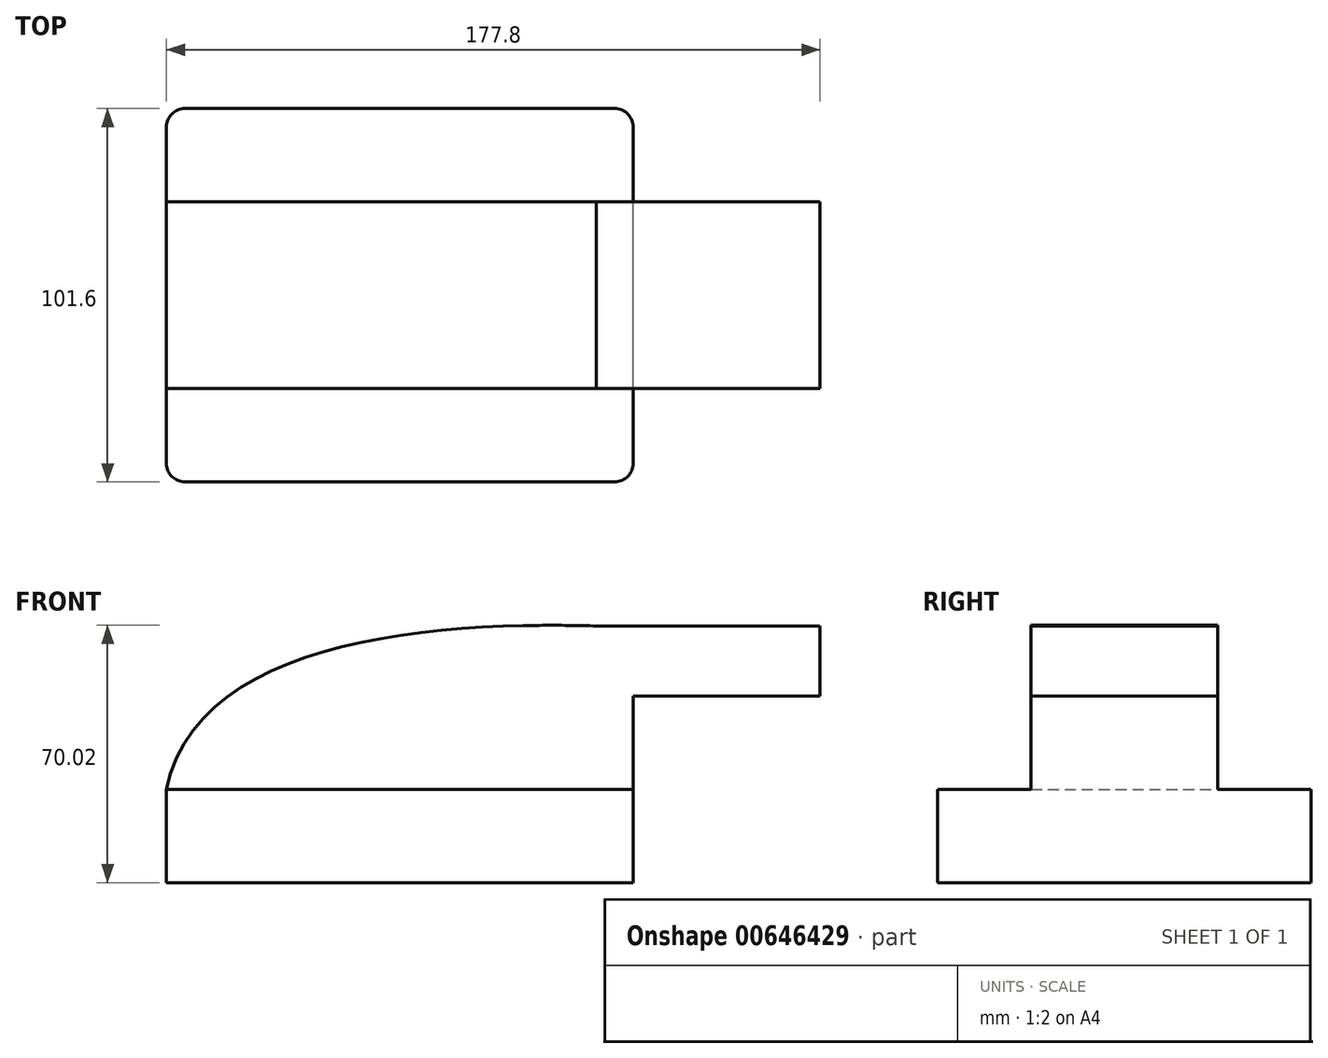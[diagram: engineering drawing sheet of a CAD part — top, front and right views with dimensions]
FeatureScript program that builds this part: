
annotation { "Feature Type Name" : "Feature", "Feature Type Description" : "" }
export const myFeature = defineFeature(function(context is Context, id is Id, definition is map)
    precondition{}
    {
        {
            var Q0;
            Q0=qCreatedBy(makeId("Front.planeOp"),FACE);
            var sketch = newSketch(context, id + "F0", { "sketchPlane" : qUnion([Q0])});
            skLineSegment(sketch, "E0.bottom", {"start": v(-65.41, 0) * mm, "end": v(61.59, 0) * mm});
            skLineSegment(sketch, "E0.top", {"start": v(-65.41, 25.4) * mm, "end": v(61.59, 25.4) * mm});
            skLineSegment(sketch, "E0.left", {"start": v(-65.41, 0) * mm, "end": v(-65.41, 25.4) * mm});
            skLineSegment(sketch, "E0.right", {"start": v(61.59, 0) * mm, "end": v(61.59, 25.4) * mm});
            skLineSegment(sketch, "E1.bottom", {"start": v(61.59, 25.4) * mm, "end": v(36.19, 25.4) * mm});
            skLineSegment(sketch, "E1.top", {"start": v(61.59, 50.8) * mm, "end": v(36.19, 50.8) * mm});
            skLineSegment(sketch, "E1.left", {"start": v(61.59, 25.4) * mm, "end": v(61.59, 50.8) * mm});
            skLineSegment(sketch, "E1.right", {"start": v(36.19, 25.4) * mm, "end": v(36.19, 50.8) * mm});
            skArc(sketch, "E2", {"start": v(-8.59, 25.4) * mm, "mid": v(4.52, 57.06) * mm, "end": v(36.19, 70.18) * mm});
            skLineSegment(sketch, "E3.bottom", {"start": v(36.19, 50.8) * mm, "end": v(112.39, 50.8) * mm});
            skLineSegment(sketch, "E3.top", {"start": v(36.19, 69.85) * mm, "end": v(112.39, 69.85) * mm});
            skLineSegment(sketch, "E3.left", {"start": v(36.19, 50.8) * mm, "end": v(36.19, 69.85) * mm});
            skLineSegment(sketch, "E3.right", {"start": v(112.39, 50.8) * mm, "end": v(112.39, 69.85) * mm});
            skFitSpline(sketch, "E4", {"points": [v(51.46, 69.85) * mm, v(-65.41, 25.4) * mm], "startDerivative": vector(-135.2, 3.84) * mm, "endDerivative": vector(-24.95, -122.3) * mm});
            skSolve(sketch);
        }
        {
            var Q0;
            Q0=makeQuery(id+"F0.imprint","IMPRINT",FACE,{"disambiguationData":[TD([[makeQuery(id+"F0.imprint","IMPRINT",EDGE,{"derivedFrom":sQuery(id+"F0.wireOp",EDGE,"E0.bottom")}),1.0]])]});
            extrude(context, id + "F1", {"entities" : qUnion([Q0]), "depth" : 50.8 * mm, "offsetDistance" : 25.4 * mm, "hasSecondDirection" : true, "secondDirectionOppositeDirection" : true, "secondDirectionDepth" : 50.8 * mm});
        }
        {
            var Q0;
            Q0=makeQuery(id+"F1.opExtrude","CAP_EDGE",EDGE,{"disambiguationData":[OSD([sQuery(id+"F0.wireOp",EDGE,"E0.right")])],"isStart":false});
            var Q1;
            Q1=makeQuery(id+"F1.opExtrude","CAP_EDGE",EDGE,{"disambiguationData":[OSD([sQuery(id+"F0.wireOp",EDGE,"E0.right")])],"isStart":true});
            var Q2;
            Q2=makeQuery(id+"F1.opExtrude","CAP_EDGE",EDGE,{"disambiguationData":[OSD([sQuery(id+"F0.wireOp",EDGE,"E0.left")])],"isStart":true});
            var Q3;
            Q3=makeQuery(id+"F1.opExtrude","CAP_EDGE",EDGE,{"disambiguationData":[OSD([sQuery(id+"F0.wireOp",EDGE,"E0.left")])],"isStart":false});
            fillet(context, id + "F2", {"entities" : qUnion([Q0, Q1, Q2, Q3]), "radius" : 5.08 * mm, "tangentPropagation" : true, "allowEdgeOverflow" : false});
        }
        {
            var Q0;
            Q0 = qSketchRegion(id + "F0", true);
            extrude(context, id + "F3", {"entities" : qUnion([Q0]), "operationType" : NewBodyOperationType.ADD, "depth" : 25.4 * mm, "offsetDistance" : 25.4 * mm, "hasSecondDirection" : true, "secondDirectionOppositeDirection" : true, "secondDirectionDepth" : 25.4 * mm});
        }
    });
